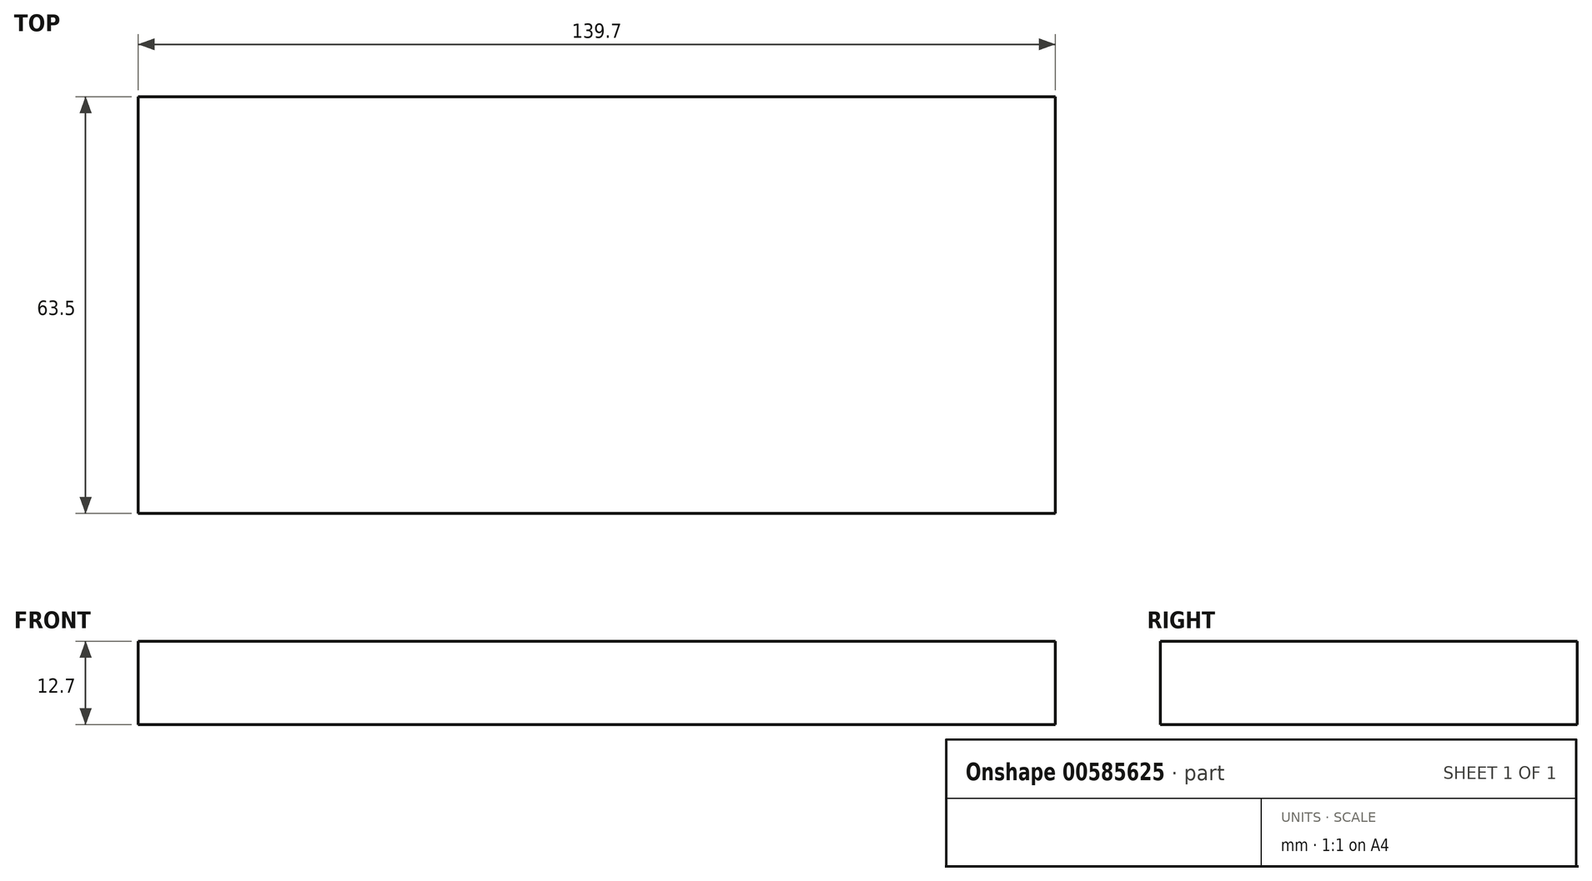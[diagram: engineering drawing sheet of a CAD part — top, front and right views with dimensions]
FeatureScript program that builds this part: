
annotation { "Feature Type Name" : "Feature", "Feature Type Description" : "" }
export const myFeature = defineFeature(function(context is Context, id is Id, definition is map)
    precondition{}
    {
        {
            var Q0;
            Q0=qCreatedBy(makeId("Top.planeOp"),FACE);
            var sketch = newSketch(context, id + "F0", { "sketchPlane" : qUnion([Q0])});
            skLineSegment(sketch, "E0.bottom", {"start": v(-69.85, 31.75) * mm, "end": v(69.85, 31.75) * mm});
            skLineSegment(sketch, "E0.top", {"start": v(-69.85, -31.75) * mm, "end": v(69.85, -31.75) * mm});
            skLineSegment(sketch, "E0.left", {"start": v(-69.85, 31.75) * mm, "end": v(-69.85, -31.75) * mm});
            skLineSegment(sketch, "E0.right", {"start": v(69.85, 31.75) * mm, "end": v(69.85, -31.75) * mm});
            skPoint(sketch, "E0.middle", {"position": v(0, 0) * mm});
            skSolve(sketch);
        }
        {
            var Q0;
            Q0=makeQuery(id+"F0.imprint","IMPRINT",FACE,{"disambiguationData":[TD([[makeQuery(id+"F0.imprint","IMPRINT",EDGE,{"derivedFrom":sQuery(id+"F0.wireOp",EDGE,"E0.bottom")}),-1.0]])]});
            extrude(context, id + "F1", {"entities" : qUnion([Q0]), "depth" : 12.7 * mm, "offsetDistance" : 25.4 * mm});
        }
    });
